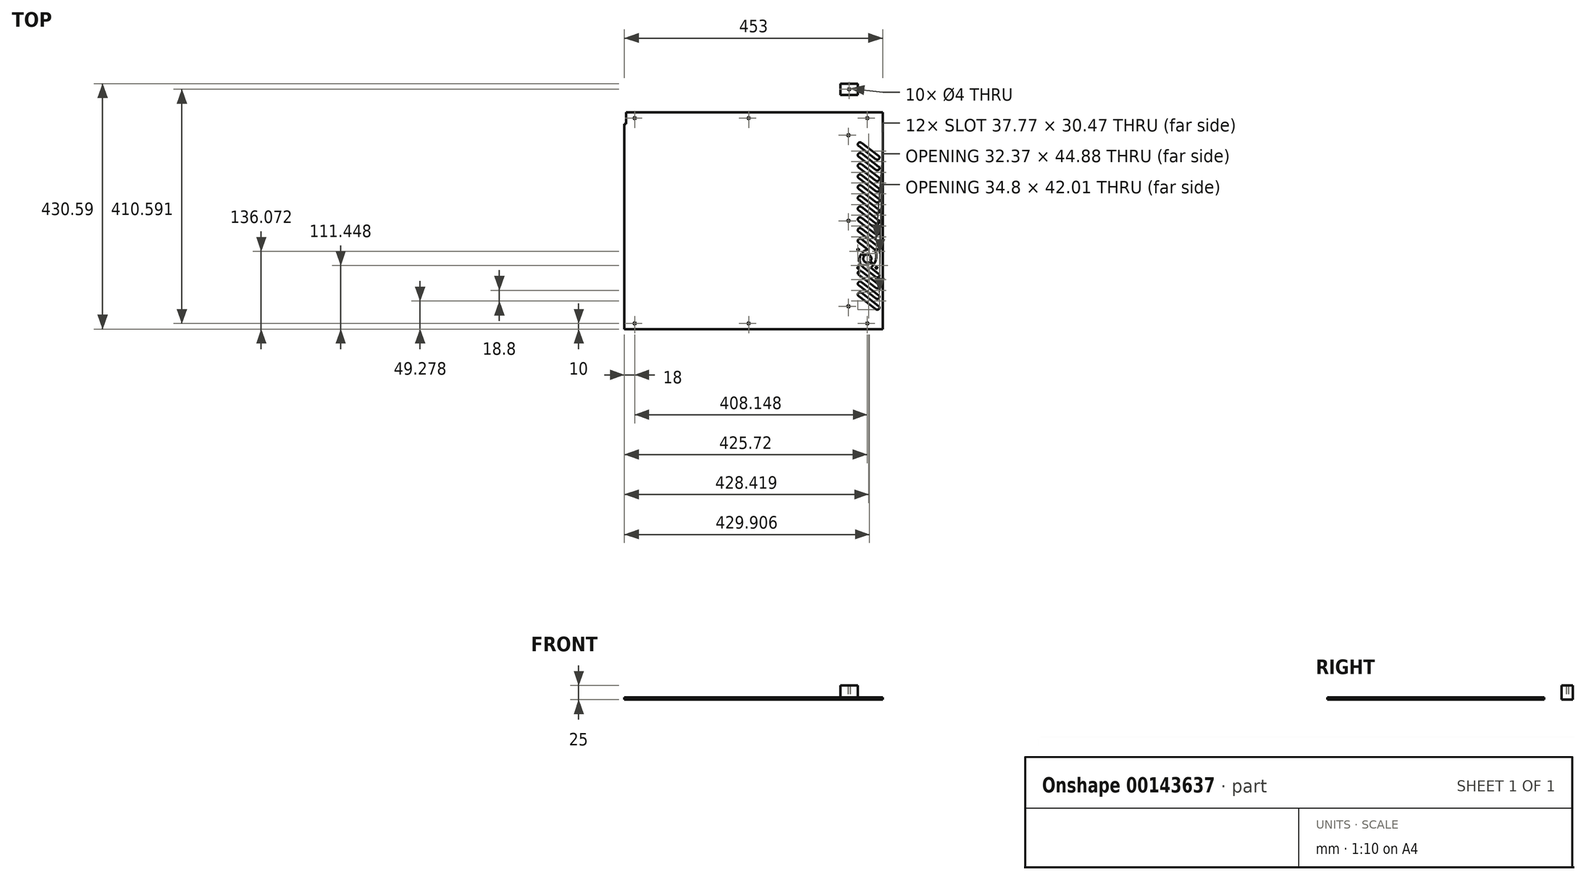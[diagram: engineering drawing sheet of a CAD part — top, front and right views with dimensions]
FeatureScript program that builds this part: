
annotation { "Feature Type Name" : "Feature", "Feature Type Description" : "" }
export const myFeature = defineFeature(function(context is Context, id is Id, definition is map)
    precondition{}
    {
        {
            var Q0;
            Q0=qCreatedBy(makeId("Top.planeOp"),FACE);
            var sketch = newSketch(context, id + "F0", { "sketchPlane" : qUnion([Q0])});
            skLineSegment(sketch, "E0.bottom", {"start": v(-215, 190) * mm, "end": v(235, 190) * mm});
            skLineSegment(sketch, "E0.top", {"start": v(-218, -190) * mm, "end": v(235, -190) * mm});
            skPoint(sketch, "E0.middle", {"position": v(0, 0) * mm});
            skLineSegment(sketch, "E1.bottom", {"start": v(-218, -190) * mm, "end": v(-215, -190) * mm});
            skLineSegment(sketch, "E1.top", {"start": v(-218, -170) * mm, "end": v(-215, -170) * mm});
            skLineSegment(sketch, "E1.right", {"start": v(-215, -190) * mm, "end": v(-215, -170) * mm, "construction": true});
            skLineSegment(sketch, "E2", {"start": v(-235, 0) * mm, "end": v(-137.24, 0) * mm, "construction": true});
            skLineSegment(sketch, "E3", {"start": v(-137.24, 0) * mm, "end": v(0, -190) * mm, "construction": true});
            skLineSegment(sketch, "E4", {"start": v(0, -190) * mm, "end": v(0, 0) * mm, "construction": true});
            skLineSegment(sketch, "E5.MirrorCS", {"start": v(-215, 190) * mm, "end": v(-215, 170) * mm});
            skLineSegment(sketch, "E6.MirrorCS", {"start": v(-218, 170) * mm, "end": v(-215, 170) * mm});
            skLineSegment(sketch, "E7.MirrorCS", {"start": v(215, 190) * mm, "end": v(215, 170) * mm, "construction": true});
            skLineSegment(sketch, "E8.MirrorCS", {"start": v(235, 170) * mm, "end": v(215, 170) * mm, "construction": true});
            skLineSegment(sketch, "E9.MirrorCS", {"start": v(215, -190) * mm, "end": v(215, -170) * mm, "construction": true});
            skLineSegment(sketch, "E10.MirrorCS", {"start": v(235, -170) * mm, "end": v(215, -170) * mm, "construction": true});
            skLineSegment(sketch, "E11", {"start": v(-215, -170) * mm, "end": v(215, -170) * mm, "construction": true});
            skLineSegment(sketch, "E12", {"start": v(-215, -170) * mm, "end": v(-215, 170) * mm, "construction": true});
            skLineSegment(sketch, "E13", {"start": v(-218, 170) * mm, "end": v(-218, -190) * mm});
            skPoint(sketch, "E14.orphan", {"position": v(-235, 170) * mm});
            skPoint(sketch, "E15.orphan", {"position": v(-235, 190) * mm});
            skPoint(sketch, "E16", {"position": v(175, -190) * mm});
            skLineSegment(sketch, "E17", {"start": v(175, -190) * mm, "end": v(175, -170) * mm, "construction": true});
            skLineSegment(sketch, "E18", {"start": v(175, -170) * mm, "end": v(175, 0) * mm, "construction": true});
            skCircle(sketch, "E19", {"center": v(175, 0) * mm, "radius": 2 * mm});
            skCircle(sketch, "E20", {"center": v(175, -150) * mm, "radius": 2 * mm});
            skLineSegment(sketch, "E21", {"start": v(-215, -180) * mm, "end": v(0, -180) * mm, "construction": true});
            skLineSegment(sketch, "E22", {"start": v(175, -180) * mm, "end": v(241.3, -180) * mm, "construction": true});
            skCircle(sketch, "E23", {"center": v(208.15, -180) * mm, "radius": 2 * mm});
            skLineSegment(sketch, "E24", {"start": v(0, -180) * mm, "end": v(175, -180) * mm, "construction": true});
            skCircle(sketch, "E25", {"center": v(0, -180) * mm, "radius": 2 * mm});
            skCircle(sketch, "E26", {"center": v(-200, -180) * mm, "radius": 2 * mm});
            skCircle(sketch, "E27.MirrorC", {"center": v(-200, 180) * mm, "radius": 2 * mm});
            skCircle(sketch, "E28.MirrorC", {"center": v(0, 180) * mm, "radius": 2 * mm});
            skLineSegment(sketch, "E29.MirrorCS", {"start": v(0, 180) * mm, "end": v(175, 180) * mm, "construction": true});
            skCircle(sketch, "E30.MirrorC", {"center": v(208.15, 180) * mm, "radius": 2 * mm});
            skCircle(sketch, "E31.MirrorC", {"center": v(175, 150) * mm, "radius": 2 * mm});
            skLineSegment(sketch, "E32", {"start": v(235, -190) * mm, "end": v(235, 190) * mm});
            skLineSegment(sketch, "E33.bottom", {"start": v(224.15, -50.4) * mm, "end": v(192.15, -50.4) * mm, "construction": true});
            skLineSegment(sketch, "E33.top", {"start": v(224.15, -82.4) * mm, "end": v(192.15, -82.4) * mm, "construction": true});
            skLineSegment(sketch, "E33.left", {"start": v(224.15, -50.4) * mm, "end": v(224.15, -82.4) * mm, "construction": true});
            skLineSegment(sketch, "E33.right", {"start": v(192.15, -50.4) * mm, "end": v(192.15, -82.4) * mm, "construction": true});
            skPoint(sketch, "E33.middle", {"position": v(208.15, -66.4) * mm});
            skCircle(sketch, "E34", {"center": v(192.15, -50.4) * mm, "radius": 1.5 * mm});
            skCircle(sketch, "E35", {"center": v(224.15, -50.4) * mm, "radius": 1.5 * mm});
            skCircle(sketch, "E36", {"center": v(224.15, -82.4) * mm, "radius": 1.5 * mm});
            skCircle(sketch, "E37", {"center": v(192.15, -82.4) * mm, "radius": 1.5 * mm});
            skLineSegment(sketch, "E38.bottom", {"start": v(227.88, -149.22) * mm, "end": v(197.59, -126.22) * mm});
            skPoint(sketch, "E38.middle", {"position": v(208.15, -129.18) * mm});
            skArc(sketch, "E39", {"start": v(197.59, -126.22) * mm, "mid": v(192.27, -126.95) * mm, "end": v(193, -132.27) * mm});
            skArc(sketch, "E40", {"start": v(223.3, -155.26) * mm, "mid": v(228.56, -154.5) * mm, "end": v(227.88, -149.22) * mm});
            skLineSegment(sketch, "E41", {"start": v(193, -132.27) * mm, "end": v(223.3, -155.26) * mm});
            skArc(sketch, "E42.0.1.0", {"start": v(197.59, -107.42) * mm, "mid": v(192.27, -108.15) * mm, "end": v(193, -113.47) * mm});
            skLineSegment(sketch, "E42.0.1.1", {"start": v(193, -113.47) * mm, "end": v(223.3, -136.46) * mm});
            skLineSegment(sketch, "E42.0.1.2", {"start": v(227.88, -130.42) * mm, "end": v(197.59, -107.42) * mm});
            skArc(sketch, "E42.0.1.3", {"start": v(223.3, -136.46) * mm, "mid": v(228.56, -135.7) * mm, "end": v(227.88, -130.42) * mm});
            skArc(sketch, "E42.0.2.0", {"start": v(197.59, -88.62) * mm, "mid": v(192.27, -89.35) * mm, "end": v(193, -94.67) * mm});
            skLineSegment(sketch, "E42.0.2.1", {"start": v(193, -94.67) * mm, "end": v(223.3, -117.66) * mm});
            skLineSegment(sketch, "E42.0.2.2", {"start": v(227.88, -111.62) * mm, "end": v(197.59, -88.62) * mm});
            skArc(sketch, "E42.0.2.3", {"start": v(223.3, -117.66) * mm, "mid": v(228.56, -116.9) * mm, "end": v(227.88, -111.62) * mm});
            skLineSegment(sketch, "E42.0.3.1", {"start": v(201.6, -82.4) * mm, "end": v(223.3, -98.86) * mm});
            skLineSegment(sketch, "E42.0.3.2", {"start": v(227.88, -92.82) * mm, "end": v(214.16, -82.4) * mm});
            skArc(sketch, "E42.0.3.3", {"start": v(223.3, -98.86) * mm, "mid": v(228.56, -98.1) * mm, "end": v(227.88, -92.82) * mm});
            skArc(sketch, "E42.0.5.0", {"start": v(197.59, -32.22) * mm, "mid": v(192.27, -32.95) * mm, "end": v(193, -38.27) * mm});
            skLineSegment(sketch, "E42.0.5.1", {"start": v(193, -38.27) * mm, "end": v(208.99, -50.4) * mm});
            skArc(sketch, "E42.0.6.0", {"start": v(197.59, -13.42) * mm, "mid": v(192.27, -14.15) * mm, "end": v(193, -19.47) * mm});
            skLineSegment(sketch, "E42.0.6.1", {"start": v(193, -19.47) * mm, "end": v(223.3, -42.46) * mm});
            skLineSegment(sketch, "E42.0.6.2", {"start": v(227.88, -36.42) * mm, "end": v(197.59, -13.42) * mm});
            skArc(sketch, "E42.0.6.3", {"start": v(223.3, -42.46) * mm, "mid": v(228.56, -41.7) * mm, "end": v(227.88, -36.42) * mm});
            skArc(sketch, "E42.0.7.0", {"start": v(197.59, 5.38) * mm, "mid": v(192.27, 4.65) * mm, "end": v(193, -0.67) * mm});
            skLineSegment(sketch, "E42.0.7.1", {"start": v(193, -0.67) * mm, "end": v(223.3, -23.66) * mm});
            skLineSegment(sketch, "E42.0.7.2", {"start": v(227.88, -17.62) * mm, "end": v(197.59, 5.38) * mm});
            skArc(sketch, "E42.0.7.3", {"start": v(223.3, -23.66) * mm, "mid": v(228.56, -22.9) * mm, "end": v(227.88, -17.62) * mm});
            skArc(sketch, "E42.0.8.0", {"start": v(197.59, 24.18) * mm, "mid": v(192.27, 23.45) * mm, "end": v(193, 18.13) * mm});
            skLineSegment(sketch, "E42.0.8.1", {"start": v(193, 18.13) * mm, "end": v(223.3, -4.86) * mm});
            skLineSegment(sketch, "E42.0.8.2", {"start": v(227.88, 1.18) * mm, "end": v(197.59, 24.18) * mm});
            skArc(sketch, "E42.0.8.3", {"start": v(223.3, -4.86) * mm, "mid": v(228.56, -4.1) * mm, "end": v(227.88, 1.18) * mm});
            skArc(sketch, "E42.0.9.0", {"start": v(197.59, 42.98) * mm, "mid": v(192.27, 42.25) * mm, "end": v(193, 36.93) * mm});
            skLineSegment(sketch, "E42.0.9.1", {"start": v(193, 36.93) * mm, "end": v(223.3, 13.94) * mm});
            skLineSegment(sketch, "E42.0.9.2", {"start": v(227.88, 19.98) * mm, "end": v(197.59, 42.98) * mm});
            skArc(sketch, "E42.0.9.3", {"start": v(223.3, 13.94) * mm, "mid": v(228.56, 14.7) * mm, "end": v(227.88, 19.98) * mm});
            skArc(sketch, "E42.0.10.0", {"start": v(197.59, 61.78) * mm, "mid": v(192.27, 61.05) * mm, "end": v(193, 55.73) * mm});
            skLineSegment(sketch, "E42.0.10.1", {"start": v(193, 55.73) * mm, "end": v(223.3, 32.74) * mm});
            skLineSegment(sketch, "E42.0.10.2", {"start": v(227.88, 38.78) * mm, "end": v(197.59, 61.78) * mm});
            skArc(sketch, "E42.0.10.3", {"start": v(223.3, 32.74) * mm, "mid": v(228.56, 33.5) * mm, "end": v(227.88, 38.78) * mm});
            skArc(sketch, "E42.0.11.0", {"start": v(197.59, 80.58) * mm, "mid": v(192.27, 79.85) * mm, "end": v(193, 74.53) * mm});
            skLineSegment(sketch, "E42.0.11.1", {"start": v(193, 74.53) * mm, "end": v(223.3, 51.54) * mm});
            skLineSegment(sketch, "E42.0.11.2", {"start": v(227.88, 57.58) * mm, "end": v(197.59, 80.58) * mm});
            skArc(sketch, "E42.0.11.3", {"start": v(223.3, 51.54) * mm, "mid": v(228.56, 52.3) * mm, "end": v(227.88, 57.58) * mm});
            skArc(sketch, "E42.0.12.0", {"start": v(197.59, 99.38) * mm, "mid": v(192.27, 98.65) * mm, "end": v(193, 93.33) * mm});
            skLineSegment(sketch, "E42.0.12.1", {"start": v(193, 93.33) * mm, "end": v(223.3, 70.34) * mm});
            skLineSegment(sketch, "E42.0.12.2", {"start": v(227.88, 76.38) * mm, "end": v(197.59, 99.38) * mm});
            skArc(sketch, "E42.0.12.3", {"start": v(223.3, 70.34) * mm, "mid": v(228.56, 71.1) * mm, "end": v(227.88, 76.38) * mm});
            skArc(sketch, "E42.0.13.0", {"start": v(197.59, 118.18) * mm, "mid": v(192.27, 117.45) * mm, "end": v(193, 112.13) * mm});
            skLineSegment(sketch, "E42.0.13.1", {"start": v(193, 112.13) * mm, "end": v(223.3, 89.14) * mm});
            skLineSegment(sketch, "E42.0.13.2", {"start": v(227.88, 95.18) * mm, "end": v(197.59, 118.18) * mm});
            skArc(sketch, "E42.0.13.3", {"start": v(223.3, 89.14) * mm, "mid": v(228.56, 89.9) * mm, "end": v(227.88, 95.18) * mm});
            skArc(sketch, "E42.0.14.0", {"start": v(197.59, 136.98) * mm, "mid": v(192.27, 136.25) * mm, "end": v(193, 130.93) * mm});
            skLineSegment(sketch, "E42.0.14.1", {"start": v(193, 130.93) * mm, "end": v(223.3, 107.94) * mm});
            skLineSegment(sketch, "E42.0.14.2", {"start": v(227.88, 113.98) * mm, "end": v(197.59, 136.98) * mm});
            skArc(sketch, "E42.0.14.3", {"start": v(223.3, 107.94) * mm, "mid": v(228.56, 108.7) * mm, "end": v(227.88, 113.98) * mm});
            skLineSegment(sketch, "E42.direction1", {"start": v(193, -132.27) * mm, "end": v(218, -132.27) * mm, "construction": true});
            skLineSegment(sketch, "E42.direction2", {"start": v(193, -132.27) * mm, "end": v(193, -113.47) * mm, "construction": true});
            skPoint(sketch, "E43", {"position": v(208.15, -68.56) * mm});
            skLineSegment(sketch, "E44.trimOffspring", {"start": v(221.54, -50.4) * mm, "end": v(197.59, -32.22) * mm});
            skArc(sketch, "E45", {"start": v(208.99, -50.4) * mm, "mid": v(203.62, -52.4) * mm, "end": v(199.14, -55.98) * mm});
            skArc(sketch, "E46", {"start": v(213.83, -70.67) * mm, "mid": v(213.18, -61.37) * mm, "end": v(203.88, -60.72) * mm});
            skArc(sketch, "E47", {"start": v(214.16, -82.4) * mm, "mid": v(216.38, -80.33) * mm, "end": v(218.36, -78.03) * mm});
            skLineSegment(sketch, "E48.0", {"start": v(224.15, -80.99) * mm, "end": v(224.06, -80.9) * mm});
            skLineSegment(sketch, "E49.0", {"start": v(222.73, -82.4) * mm, "end": v(222.65, -82.32) * mm});
            skLineSegment(sketch, "E50.trimOffspring", {"start": v(192.23, -51.9) * mm, "end": v(192.15, -51.82) * mm});
            skLineSegment(sketch, "E51.trimOffspring", {"start": v(193.65, -50.48) * mm, "end": v(193.56, -50.4) * mm});
            skLineSegment(sketch, "E52.trimOffspring", {"start": v(218.36, -78.03) * mm, "end": v(212.42, -72.09) * mm});
            skLineSegment(sketch, "E53.trimOffspring", {"start": v(219.53, -76.37) * mm, "end": v(213.83, -70.67) * mm});
            skLineSegment(sketch, "E54.trimOffspring", {"start": v(202.46, -62.13) * mm, "end": v(197.88, -57.55) * mm});
            skLineSegment(sketch, "E55.trimOffspring", {"start": v(203.88, -60.72) * mm, "end": v(199.14, -55.98) * mm});
            skArc(sketch, "E56.trimOffspring", {"start": v(202.46, -62.13) * mm, "mid": v(203.12, -71.43) * mm, "end": v(212.42, -72.09) * mm});
            skArc(sketch, "E57.trimOffspring", {"start": v(197.88, -57.55) * mm, "mid": v(194.69, -70.73) * mm, "end": v(201.6, -82.4) * mm});
            skArc(sketch, "E58.trimOffspring", {"start": v(219.53, -76.37) * mm, "mid": v(223.86, -63.64) * mm, "end": v(221.54, -50.4) * mm});
            skLineSegment(sketch, "E59.bottom", {"start": v(161.2, 240.6) * mm, "end": v(191.2, 240.6) * mm});
            skLineSegment(sketch, "E59.top", {"start": v(161.2, 220.6) * mm, "end": v(191.2, 220.6) * mm});
            skLineSegment(sketch, "E59.left", {"start": v(161.2, 240.6) * mm, "end": v(161.2, 220.6) * mm});
            skLineSegment(sketch, "E59.right", {"start": v(191.2, 240.6) * mm, "end": v(191.2, 220.6) * mm});
            skCircle(sketch, "E60", {"center": v(176.2, 230.6) * mm, "radius": 2 * mm});
            skPoint(sketch, "E60.centerSnap0", {"position": v(176.2, 240.6) * mm});
            skPoint(sketch, "E60.centerSnap1", {"position": v(161.2, 230.6) * mm});
            skSolve(sketch);
        }
        {
            var Q0;
            Q0=makeQuery(id+"F0.imprint","IMPRINT",FACE,{"disambiguationData":[TD([[makeQuery(id+"F0.imprint","IMPRINT",EDGE,{"derivedFrom":sQuery(id+"F0.wireOp",EDGE,"E0.bottom")}),-1.0]])]});
            extrude(context, id + "F1", {"entities" : qUnion([Q0]), "depth" : 4 * mm});
        }
        {
            var Q0;
            Q0=makeQuery(id+"F0.imprint","IMPRINT",FACE,{"disambiguationData":[TD([[makeQuery(id+"F0.imprint","IMPRINT",EDGE,{"derivedFrom":sQuery(id+"F0.wireOp",EDGE,"E59.bottom")}),-1.0]])]});
            extrude(context, id + "F2", {"entities" : qUnion([Q0]), "depth" : 25 * mm});
        }
    });
